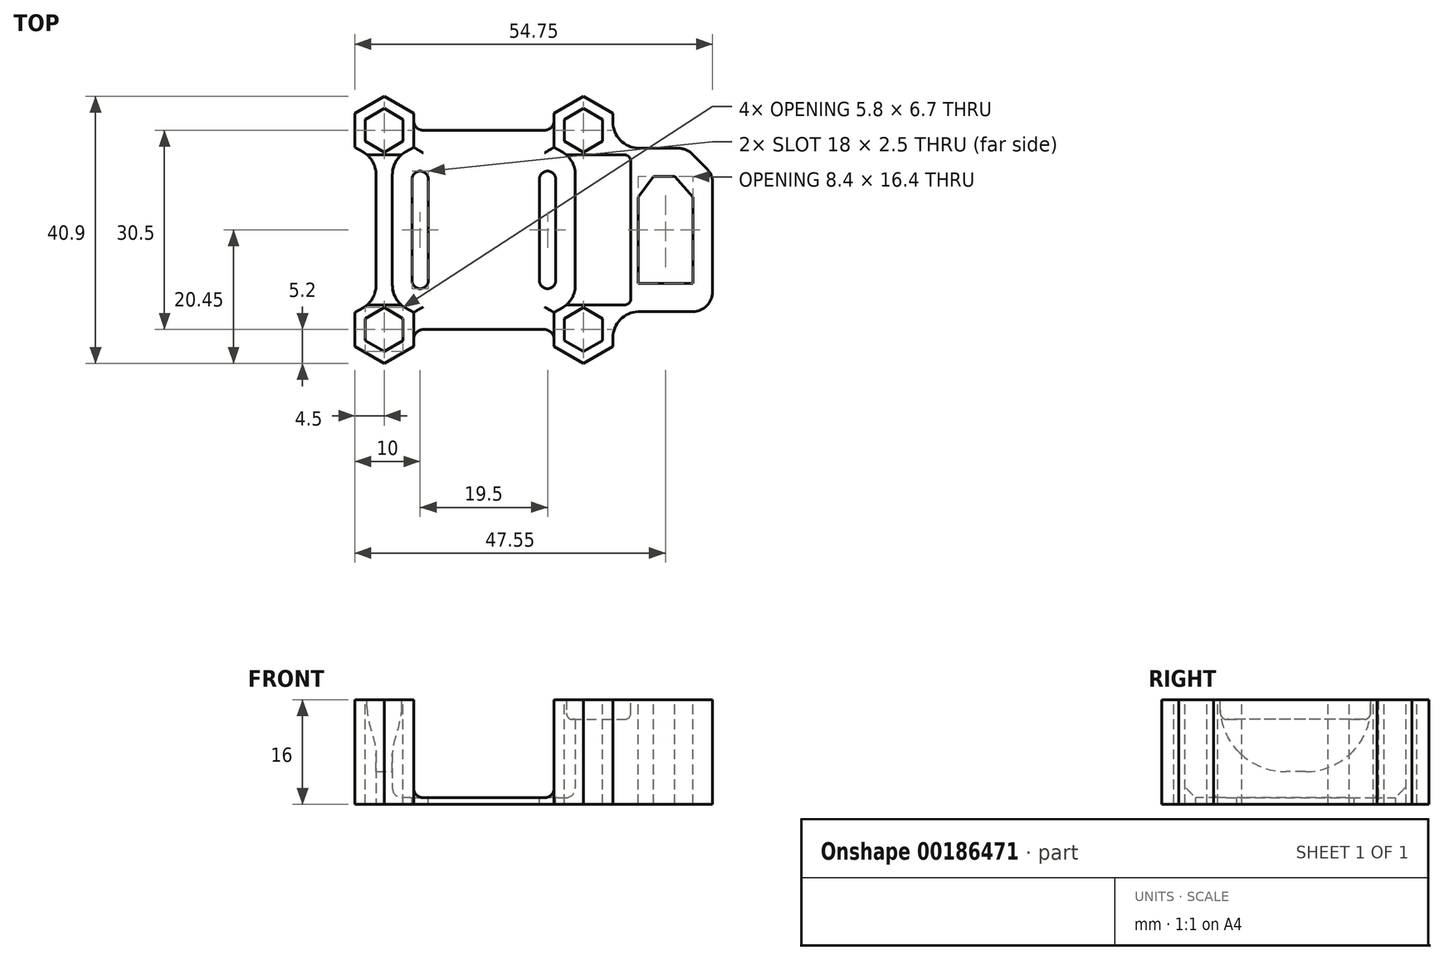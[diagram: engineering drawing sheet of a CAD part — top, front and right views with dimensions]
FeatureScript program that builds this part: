
annotation { "Feature Type Name" : "Feature", "Feature Type Description" : "" }
export const myFeature = defineFeature(function(context is Context, id is Id, definition is map)
    precondition{}
    {
        {
            var Q0;
            Q0=qCreatedBy(makeId("Top.planeOp"),FACE);
            var sketch = newSketch(context, id + "F0", { "sketchPlane" : qUnion([Q0])});
            skLineSegment(sketch, "E0.bottom", {"start": v(-15.25, 15.25) * mm, "end": v(15.25, 15.25) * mm});
            skLineSegment(sketch, "E0.top", {"start": v(-15.25, -15.25) * mm, "end": v(15.25, -15.25) * mm});
            skLineSegment(sketch, "E0.left", {"start": v(-15.25, 15.25) * mm, "end": v(-15.25, -15.25) * mm});
            skLineSegment(sketch, "E0.right", {"start": v(15.25, 15.25) * mm, "end": v(15.25, -15.25) * mm});
            skSolve(sketch);
        }
        {
            var Q0;
            Q0 = qSketchRegion(id + "F0", true);
            extrude(context, id + "F1", {"entities" : qUnion([Q0]), "depth" : 1 * mm});
        }
        {
            var Q0;
            Q0=qCreatedBy(makeId("Top.planeOp"),FACE);
            var sketch = newSketch(context, id + "F2", { "sketchPlane" : qUnion([Q0])});
            skCircle(sketch, "E1.cCircle", {"center": v(-15.25, 15.25) * mm, "radius": 4.5 * mm, "construction": true});
            skLineSegment(sketch, "E1.0", {"start": v(-16.5, 10.78) * mm, "end": v(-19.75, 12.65) * mm});
            skLineSegment(sketch, "E1.1", {"start": v(-19.75, 12.65) * mm, "end": v(-19.75, 17.85) * mm});
            skLineSegment(sketch, "E1.2", {"start": v(-19.75, 17.85) * mm, "end": v(-15.25, 20.45) * mm});
            skLineSegment(sketch, "E1.3", {"start": v(-15.25, 20.45) * mm, "end": v(-10.75, 17.85) * mm});
            skLineSegment(sketch, "E1.4", {"start": v(-10.75, 17.85) * mm, "end": v(-10.75, 12.65) * mm});
            skLineSegment(sketch, "E1.5", {"start": v(-10.75, 12.65) * mm, "end": v(-14, 10.78) * mm});
            skPoint(sketch, "E1.0.midPoint", {"position": v(-17.5, 11.35) * mm});
            skCircle(sketch, "E2.MirrorC", {"center": v(15.25, 15.25) * mm, "radius": 4.5 * mm, "construction": true});
            skLineSegment(sketch, "E3.MirrorCS", {"start": v(19.75, 12.65) * mm, "end": v(19.75, 17.85) * mm});
            skLineSegment(sketch, "E4.MirrorCS", {"start": v(19.75, 17.85) * mm, "end": v(15.25, 20.45) * mm});
            skLineSegment(sketch, "E5.MirrorCS", {"start": v(15.25, 20.45) * mm, "end": v(10.75, 17.85) * mm});
            skLineSegment(sketch, "E6.MirrorCS", {"start": v(10.75, 17.85) * mm, "end": v(10.75, 12.65) * mm});
            skLineSegment(sketch, "E7.MirrorCS", {"start": v(10.75, 12.65) * mm, "end": v(14, 10.78) * mm});
            skPoint(sketch, "E8.MirrorP", {"position": v(17.5, 11.35) * mm});
            skLineSegment(sketch, "E9.MirrorCS", {"start": v(-16.5, -10.78) * mm, "end": v(-19.75, -12.65) * mm});
            skLineSegment(sketch, "E10.MirrorCS", {"start": v(-19.75, -12.65) * mm, "end": v(-19.75, -17.85) * mm});
            skLineSegment(sketch, "E11.MirrorCS", {"start": v(10.75, -17.85) * mm, "end": v(10.75, -12.65) * mm});
            skLineSegment(sketch, "E12.MirrorCS", {"start": v(10.75, -12.65) * mm, "end": v(14, -10.78) * mm});
            skLineSegment(sketch, "E13.MirrorCS", {"start": v(-19.75, -17.85) * mm, "end": v(-15.25, -20.45) * mm});
            skLineSegment(sketch, "E14.MirrorCS", {"start": v(15.25, -20.45) * mm, "end": v(10.75, -17.85) * mm});
            skLineSegment(sketch, "E15.MirrorCS", {"start": v(-15.25, -20.45) * mm, "end": v(-10.75, -17.85) * mm});
            skLineSegment(sketch, "E16.MirrorCS", {"start": v(19.75, -17.85) * mm, "end": v(15.25, -20.45) * mm});
            skLineSegment(sketch, "E17.MirrorCS", {"start": v(-10.75, -17.85) * mm, "end": v(-10.75, -12.65) * mm});
            skLineSegment(sketch, "E18.MirrorCS", {"start": v(19.75, -12.65) * mm, "end": v(19.75, -17.85) * mm});
            skCircle(sketch, "E19.MirrorC", {"center": v(-15.25, -15.25) * mm, "radius": 4.5 * mm, "construction": true});
            skCircle(sketch, "E20.MirrorC", {"center": v(15.25, -15.25) * mm, "radius": 4.5 * mm, "construction": true});
            skPoint(sketch, "E21.MirrorP", {"position": v(17.5, -11.35) * mm});
            skLineSegment(sketch, "E22.MirrorCS", {"start": v(-10.75, -12.65) * mm, "end": v(-14, -10.78) * mm});
            skPoint(sketch, "E23.MirrorP", {"position": v(-17.5, -11.35) * mm});
            skLineSegment(sketch, "E24", {"start": v(-16.5, 10.78) * mm, "end": v(-16.5, -10.78) * mm});
            skLineSegment(sketch, "E25", {"start": v(-14, -10.78) * mm, "end": v(-14, 10.78) * mm});
            skLineSegment(sketch, "E26", {"start": v(14, 10.78) * mm, "end": v(14, -10.78) * mm});
            skPoint(sketch, "E27.orphan", {"position": v(-15.25, 10.05) * mm});
            skPoint(sketch, "E28.orphan", {"position": v(-15.25, -10.05) * mm});
            skPoint(sketch, "E29.orphan", {"position": v(15.25, -10.05) * mm});
            skPoint(sketch, "E30.orphan", {"position": v(15.25, 10.05) * mm});
            skLineSegment(sketch, "E31", {"start": v(24, 12.5) * mm, "end": v(24, -12.5) * mm, "construction": true});
            skLineSegment(sketch, "E32", {"start": v(24, -12.5) * mm, "end": v(19.75, -12.65) * mm});
            skLineSegment(sketch, "E33", {"start": v(24, 12.5) * mm, "end": v(19.75, 12.65) * mm});
            skLineSegment(sketch, "E34.bottom", {"start": v(24, 12.5) * mm, "end": v(35, 12.5) * mm});
            skLineSegment(sketch, "E34.top", {"start": v(24, -12.5) * mm, "end": v(35, -12.5) * mm});
            skLineSegment(sketch, "E34.right", {"start": v(35, 12.5) * mm, "end": v(35, -12.5) * mm});
            skSolve(sketch);
        }
        {
            var Q0;
            Q0 = qSketchRegion(id + "F2", true);
            extrude(context, id + "F3", {"entities" : qUnion([Q0]), "operationType" : NewBodyOperationType.ADD, "depth" : 16 * mm});
        }
        {
            var Q0;
            Q0=makeQuery(id+"F3.opExtrude","CAP_FACE",FACE,{"disambiguationData":[OSD([sQuery(id+"F2.wireOp",EDGE,"E3.MirrorCS"),sQuery(id+"F2.wireOp",EDGE,"E4.MirrorCS"),sQuery(id+"F2.wireOp",EDGE,"E5.MirrorCS"),sQuery(id+"F2.wireOp",EDGE,"E6.MirrorCS"),sQuery(id+"F2.wireOp",EDGE,"E7.MirrorCS"),sQuery(id+"F2.wireOp",EDGE,"E11.MirrorCS"),sQuery(id+"F2.wireOp",EDGE,"E12.MirrorCS"),sQuery(id+"F2.wireOp",EDGE,"E14.MirrorCS"),sQuery(id+"F2.wireOp",EDGE,"E16.MirrorCS"),sQuery(id+"F2.wireOp",EDGE,"E18.MirrorCS"),sQuery(id+"F2.wireOp",EDGE,"E26"),sQuery(id+"F2.wireOp",EDGE,"E31"),sQuery(id+"F2.wireOp",EDGE,"E32"),sQuery(id+"F2.wireOp",EDGE,"E33")])],"isStart":false});
            var sketch = newSketch(context, id + "F4", { "sketchPlane" : qUnion([Q0])});
            skLineSegment(sketch, "E35.bottom", {"start": v(-22.5, 11.5) * mm, "end": v(22.5, 11.5) * mm});
            skLineSegment(sketch, "E35.top", {"start": v(-22.5, -11.5) * mm, "end": v(22.5, -11.5) * mm});
            skLineSegment(sketch, "E35.left", {"start": v(-22.5, 11.5) * mm, "end": v(-22.5, -11.5) * mm});
            skLineSegment(sketch, "E35.right", {"start": v(22.5, 11.5) * mm, "end": v(22.5, -11.5) * mm});
            skPoint(sketch, "E36.visualSharp", {"position": v(22.5, 11.5) * mm});
            skPoint(sketch, "E37.visualSharp", {"position": v(22.5, -11.5) * mm});
            skSolve(sketch);
        }
        {
            var Q0;
            Q0 = qSketchRegion(id + "F4", true);
            extrude(context, id + "F5", {"entities" : qUnion([Q0]), "operationType" : NewBodyOperationType.REMOVE, "oppositeDirection" : true, "depth" : 3 * mm});
        }
        {
            var Q0;
            {var subQ0=sQuery(id+"F2.wireOp",EDGE,"E34.top");var subQ1=sQuery(id+"F2.wireOp",EDGE,"E34.bottom");var subQ2=sQuery(id+"F2.wireOp",EDGE,"E33");var subQ3=sQuery(id+"F2.wireOp",EDGE,"E32");var subQ4=sQuery(id+"F2.wireOp",EDGE,"E34.right");Q0=makeQuery(id+"F5.boolean.opBoolean","SPLIT",FACE,{"disambiguationData":[TD([makeQuery(id+"F3.opExtrude","SWEPT_FACE",FACE,{"disambiguationData":[OSD([subQ3])]})])],"derivedFrom":makeQuery(id+"F3.opExtrude","CAP_FACE",FACE,{"disambiguationData":[OSD([sQuery(id+"F2.wireOp",EDGE,"E3.MirrorCS"),sQuery(id+"F2.wireOp",EDGE,"E4.MirrorCS"),sQuery(id+"F2.wireOp",EDGE,"E5.MirrorCS"),sQuery(id+"F2.wireOp",EDGE,"E6.MirrorCS"),sQuery(id+"F2.wireOp",EDGE,"E7.MirrorCS"),sQuery(id+"F2.wireOp",EDGE,"E11.MirrorCS"),sQuery(id+"F2.wireOp",EDGE,"E12.MirrorCS"),sQuery(id+"F2.wireOp",EDGE,"E14.MirrorCS"),sQuery(id+"F2.wireOp",EDGE,"E16.MirrorCS"),sQuery(id+"F2.wireOp",EDGE,"E18.MirrorCS"),sQuery(id+"F2.wireOp",EDGE,"E26"),subQ3,subQ2,subQ1,subQ0,subQ4])],"isStart":false})});}
            var sketch = newSketch(context, id + "F6", { "sketchPlane" : qUnion([Q0])});
            skLineSegment(sketch, "E38.bottom", {"start": v(26, 8.2) * mm, "end": v(29.2, 8.2) * mm});
            skLineSegment(sketch, "E38.top", {"start": v(23.6, -8.2) * mm, "end": v(32, -8.2) * mm});
            skLineSegment(sketch, "E38.left", {"start": v(23.6, 5) * mm, "end": v(23.6, -8.2) * mm});
            skLineSegment(sketch, "E38.right", {"start": v(32, 5) * mm, "end": v(32, -8.2) * mm});
            skLineSegment(sketch, "E39", {"start": v(26, 8.2) * mm, "end": v(23.6, 5) * mm});
            skLineSegment(sketch, "E40", {"start": v(29.2, 8.2) * mm, "end": v(32, 5) * mm});
            skCircle(sketch, "E41.cCircle", {"center": v(-15.25, 15.25) * mm, "radius": 2.9 * mm, "construction": true});
            skLineSegment(sketch, "E41.0", {"start": v(-12.35, 13.58) * mm, "end": v(-15.25, 11.9) * mm});
            skLineSegment(sketch, "E41.1", {"start": v(-15.25, 11.9) * mm, "end": v(-18.15, 13.58) * mm});
            skLineSegment(sketch, "E41.2", {"start": v(-18.15, 13.58) * mm, "end": v(-18.15, 16.92) * mm});
            skLineSegment(sketch, "E41.3", {"start": v(-18.15, 16.92) * mm, "end": v(-15.25, 18.6) * mm});
            skLineSegment(sketch, "E41.4", {"start": v(-15.25, 18.6) * mm, "end": v(-12.35, 16.92) * mm});
            skLineSegment(sketch, "E41.5", {"start": v(-12.35, 16.92) * mm, "end": v(-12.35, 13.58) * mm});
            skPoint(sketch, "E41.0.midPoint", {"position": v(-13.8, 12.74) * mm});
            skLineSegment(sketch, "E42.0.1.0", {"start": v(-15.25, -11.9) * mm, "end": v(-12.35, -13.58) * mm});
            skLineSegment(sketch, "E42.0.1.1", {"start": v(-15.25, -18.6) * mm, "end": v(-18.15, -16.92) * mm});
            skLineSegment(sketch, "E42.0.1.2", {"start": v(-18.15, -13.58) * mm, "end": v(-15.25, -11.9) * mm});
            skPoint(sketch, "E42.0.1.3", {"position": v(-13.8, -17.76) * mm});
            skCircle(sketch, "E42.0.1.4", {"center": v(-15.25, -15.25) * mm, "radius": 2.9 * mm, "construction": true});
            skLineSegment(sketch, "E42.0.1.5", {"start": v(-12.35, -13.58) * mm, "end": v(-12.35, -16.92) * mm});
            skLineSegment(sketch, "E42.0.1.6", {"start": v(-18.15, -16.92) * mm, "end": v(-18.15, -13.58) * mm});
            skLineSegment(sketch, "E42.0.1.7", {"start": v(-12.35, -16.92) * mm, "end": v(-15.25, -18.6) * mm});
            skLineSegment(sketch, "E42.direction1", {"start": v(-18.15, 13.58) * mm, "end": v(12.35, 13.58) * mm, "construction": true});
            skLineSegment(sketch, "E42.direction2", {"start": v(-18.15, 13.58) * mm, "end": v(-18.15, -16.92) * mm, "construction": true});
            skLineSegment(sketch, "E43.MirrorCS", {"start": v(12.35, 16.92) * mm, "end": v(12.35, 13.58) * mm});
            skLineSegment(sketch, "E44.MirrorCS", {"start": v(18.15, 16.92) * mm, "end": v(15.25, 18.6) * mm});
            skLineSegment(sketch, "E45.MirrorCS", {"start": v(12.35, -16.92) * mm, "end": v(15.25, -18.6) * mm});
            skLineSegment(sketch, "E46.MirrorCS", {"start": v(18.15, 13.58) * mm, "end": v(18.15, 16.92) * mm});
            skLineSegment(sketch, "E47.MirrorCS", {"start": v(15.25, 11.9) * mm, "end": v(18.15, 13.58) * mm});
            skLineSegment(sketch, "E48.MirrorCS", {"start": v(12.35, 13.58) * mm, "end": v(15.25, 11.9) * mm});
            skLineSegment(sketch, "E49.MirrorCS", {"start": v(18.15, -13.58) * mm, "end": v(15.25, -11.9) * mm});
            skLineSegment(sketch, "E50.MirrorCS", {"start": v(15.25, -11.9) * mm, "end": v(12.35, -13.58) * mm});
            skLineSegment(sketch, "E51.MirrorCS", {"start": v(12.35, -13.58) * mm, "end": v(12.35, -16.92) * mm});
            skLineSegment(sketch, "E52.MirrorCS", {"start": v(18.15, -16.92) * mm, "end": v(18.15, -13.58) * mm});
            skLineSegment(sketch, "E53.MirrorCS", {"start": v(15.25, 18.6) * mm, "end": v(12.35, 16.92) * mm});
            skCircle(sketch, "E54.MirrorC", {"center": v(15.25, -15.25) * mm, "radius": 2.9 * mm, "construction": true});
            skLineSegment(sketch, "E55.MirrorCS", {"start": v(15.25, -18.6) * mm, "end": v(18.15, -16.92) * mm});
            skPoint(sketch, "E56.MirrorP", {"position": v(13.8, -17.76) * mm});
            skLineSegment(sketch, "E57.MirrorCS", {"start": v(18.15, 13.58) * mm, "end": v(18.15, -16.92) * mm, "construction": true});
            skPoint(sketch, "E58.MirrorP", {"position": v(13.8, 12.74) * mm});
            skCircle(sketch, "E59.MirrorC", {"center": v(15.25, 15.25) * mm, "radius": 2.9 * mm, "construction": true});
            skSolve(sketch);
        }
        {
            var Q0;
            Q0 = qSketchRegion(id + "F6", true);
            extrude(context, id + "F7", {"entities" : qUnion([Q0]), "operationType" : NewBodyOperationType.REMOVE, "endBound" : BoundingType.THROUGH_ALL, "oppositeDirection" : true, "depth" : 25 * mm});
        }
        {
            var Q0;
            Q0=makeQuery(id+"F3.opExtrude","SWEPT_EDGE",EDGE,{"disambiguationData":[OSD([sQuery(id+"F2.wireOp",EDGE,"E34.bottom"),sQuery(id+"F2.wireOp",EDGE,"E34.right")])]});
            chamfer(context, id + "F8", {"entities" : qUnion([Q0]), "width" : 4 * mm, "tangentPropagation" : true});
        }
        {
            var Q0;
            Q0=makeQuery(id+"F3.opExtrude","SWEPT_EDGE",EDGE,{"disambiguationData":[OSD([sQuery(id+"F2.wireOp",EDGE,"E1.0"),sQuery(id+"F2.wireOp",EDGE,"E24")])]});
            var Q1;
            Q1=makeQuery(id+"F3.opExtrude","SWEPT_EDGE",EDGE,{"disambiguationData":[OSD([sQuery(id+"F2.wireOp",EDGE,"E9.MirrorCS"),sQuery(id+"F2.wireOp",EDGE,"E24")])]});
            var Q2;
            Q2=makeQuery(id+"F3.opExtrude","SWEPT_EDGE",EDGE,{"disambiguationData":[OSD([sQuery(id+"F2.wireOp",EDGE,"E1.5"),sQuery(id+"F2.wireOp",EDGE,"E25")])]});
            var Q3;
            Q3=makeQuery(id+"F3.opExtrude","SWEPT_EDGE",EDGE,{"disambiguationData":[OSD([sQuery(id+"F2.wireOp",EDGE,"E22.MirrorCS"),sQuery(id+"F2.wireOp",EDGE,"E25")])]});
            var Q4;
            Q4=makeQuery(id+"F3.opExtrude","SWEPT_EDGE",EDGE,{"disambiguationData":[OSD([sQuery(id+"F2.wireOp",EDGE,"E7.MirrorCS"),sQuery(id+"F2.wireOp",EDGE,"E26")])]});
            var Q5;
            Q5=makeQuery(id+"F3.opExtrude","SWEPT_EDGE",EDGE,{"disambiguationData":[OSD([sQuery(id+"F2.wireOp",EDGE,"E12.MirrorCS"),sQuery(id+"F2.wireOp",EDGE,"E26")])]});
            var Q6;
            Q6=makeQuery(id+"F3.opExtrude","SWEPT_EDGE",EDGE,{"disambiguationData":[OSD([sQuery(id+"F2.wireOp",EDGE,"E33"),sQuery(id+"F2.wireOp",EDGE,"E34.bottom")])]});
            var Q7;
            Q7=makeQuery(id+"F3.opExtrude","SWEPT_EDGE",EDGE,{"disambiguationData":[OSD([sQuery(id+"F2.wireOp",EDGE,"E3.MirrorCS"),sQuery(id+"F2.wireOp",EDGE,"E33")])]});
            var Q8;
            Q8=makeQuery(id+"F3.opExtrude","SWEPT_EDGE",EDGE,{"disambiguationData":[OSD([sQuery(id+"F2.wireOp",EDGE,"E18.MirrorCS"),sQuery(id+"F2.wireOp",EDGE,"E32")])]});
            var Q9;
            Q9=makeQuery(id+"F3.opExtrude","SWEPT_EDGE",EDGE,{"disambiguationData":[OSD([sQuery(id+"F2.wireOp",EDGE,"E32"),sQuery(id+"F2.wireOp",EDGE,"E34.top")])]});
            fillet(context, id + "F9", {"entities" : qUnion([Q0, Q1, Q2, Q3, Q4, Q5, Q6, Q7, Q8, Q9]), "radius" : 4 * mm, "tangentPropagation" : true, "allowEdgeOverflow" : false});
        }
        {
            var Q0;
            {var subQ1=sQuery(id+"F4.wireOp",EDGE,"E35.bottom");Q0=makeQuery(id+"F5.boolean.opBoolean","COPY",EDGE,{"disambiguationData":[TD([makeQuery(id+"F3.opExtrude","SWEPT_FACE",FACE,{"disambiguationData":[OSD([sQuery(id+"F2.wireOp",EDGE,"E3.MirrorCS")])]})])],"derivedFrom":makeQuery(id+"F5.opExtrude","CAP_EDGE",EDGE,{"disambiguationData":[OSD([subQ1])],"isStart":false})});}
            var Q1;
            {var subQ0=sQuery(id+"F4.wireOp",EDGE,"E35.top");Q1=makeQuery(id+"F5.boolean.opBoolean","COPY",EDGE,{"disambiguationData":[TD([makeQuery(id+"F3.opExtrude","SWEPT_FACE",FACE,{"disambiguationData":[OSD([sQuery(id+"F2.wireOp",EDGE,"E12.MirrorCS")])]})])],"derivedFrom":makeQuery(id+"F5.opExtrude","CAP_EDGE",EDGE,{"disambiguationData":[OSD([subQ0])],"isStart":false})});}
            var Q2;
            Q2=makeQuery(id+"F5.boolean.opBoolean","COPY",EDGE,{"derivedFrom":makeQuery(id+"F5.opExtrude","CAP_EDGE",EDGE,{"disambiguationData":[OSD([sQuery(id+"F4.wireOp",EDGE,"E35.right")])],"isStart":false})});
            var Q3;
            {var subQ0=sQuery(id+"F4.wireOp",EDGE,"E35.bottom");Q3=makeQuery(id+"F5.boolean.opBoolean","COPY",EDGE,{"disambiguationData":[TD([makeQuery(id+"F3.opExtrude","SWEPT_FACE",FACE,{"disambiguationData":[OSD([sQuery(id+"F2.wireOp",EDGE,"E7.MirrorCS")])]})])],"derivedFrom":makeQuery(id+"F5.opExtrude","CAP_EDGE",EDGE,{"disambiguationData":[OSD([subQ0])],"isStart":false})});}
            fillet(context, id + "F10", {"entities" : qUnion([Q0, Q1, Q2, Q3]), "radius" : 1 * mm, "tangentPropagation" : true, "allowEdgeOverflow" : false});
        }
        {
            var Q0;
            Q0=makeQuery(id+"F9.opFillet","BLEND_EDGE",EDGE,{"blendedFrom":[makeQuery(id+"F3.opExtrude","SWEPT_EDGE",EDGE,{"disambiguationData":[OSD([sQuery(id+"F2.wireOp",EDGE,"E22.MirrorCS"),sQuery(id+"F2.wireOp",EDGE,"E25")])]}),makeQuery(id+"F1.opExtrude","CAP_FACE",FACE,{"disambiguationData":[OSD([sQuery(id+"F0.wireOp",EDGE,"E0.bottom"),sQuery(id+"F0.wireOp",EDGE,"E0.top"),sQuery(id+"F0.wireOp",EDGE,"E0.left"),sQuery(id+"F0.wireOp",EDGE,"E0.right")])],"isStart":false})],"blendedInto":[makeQuery(id+"F1.opExtrude","CAP_FACE",FACE,{"disambiguationData":[OSD([sQuery(id+"F0.wireOp",EDGE,"E0.bottom"),sQuery(id+"F0.wireOp",EDGE,"E0.top"),sQuery(id+"F0.wireOp",EDGE,"E0.left"),sQuery(id+"F0.wireOp",EDGE,"E0.right")])],"isStart":false})]});
            var Q1;
            Q1=makeQuery(id+"F3.boolean.opBoolean","INTERSECT",EDGE,{"derivedFrom":[makeQuery(id+"F1.opExtrude","CAP_FACE",FACE,{"disambiguationData":[OSD([sQuery(id+"F0.wireOp",EDGE,"E0.bottom"),sQuery(id+"F0.wireOp",EDGE,"E0.top"),sQuery(id+"F0.wireOp",EDGE,"E0.left"),sQuery(id+"F0.wireOp",EDGE,"E0.right")])],"isStart":false}),makeQuery(id+"F3.opExtrude","SWEPT_FACE",FACE,{"disambiguationData":[OSD([sQuery(id+"F2.wireOp",EDGE,"E17.MirrorCS")])]})]});
            var Q2;
            Q2=makeQuery(id+"F3.boolean.opBoolean","INTERSECT",EDGE,{"derivedFrom":[makeQuery(id+"F1.opExtrude","CAP_FACE",FACE,{"disambiguationData":[OSD([sQuery(id+"F0.wireOp",EDGE,"E0.bottom"),sQuery(id+"F0.wireOp",EDGE,"E0.top"),sQuery(id+"F0.wireOp",EDGE,"E0.left"),sQuery(id+"F0.wireOp",EDGE,"E0.right")])],"isStart":false}),makeQuery(id+"F3.opExtrude","SWEPT_FACE",FACE,{"disambiguationData":[OSD([sQuery(id+"F2.wireOp",EDGE,"E1.4")])]})]});
            var Q3;
            Q3=makeQuery(id+"F3.boolean.opBoolean","INTERSECT",EDGE,{"derivedFrom":[makeQuery(id+"F1.opExtrude","CAP_FACE",FACE,{"disambiguationData":[OSD([sQuery(id+"F0.wireOp",EDGE,"E0.bottom"),sQuery(id+"F0.wireOp",EDGE,"E0.top"),sQuery(id+"F0.wireOp",EDGE,"E0.left"),sQuery(id+"F0.wireOp",EDGE,"E0.right")])],"isStart":false}),makeQuery(id+"F3.opExtrude","SWEPT_FACE",FACE,{"disambiguationData":[OSD([sQuery(id+"F2.wireOp",EDGE,"E26")])]})]});
            var Q4;
            Q4=makeQuery(id+"F3.boolean.opBoolean","INTERSECT",EDGE,{"derivedFrom":[makeQuery(id+"F1.opExtrude","CAP_FACE",FACE,{"disambiguationData":[OSD([sQuery(id+"F0.wireOp",EDGE,"E0.bottom"),sQuery(id+"F0.wireOp",EDGE,"E0.top"),sQuery(id+"F0.wireOp",EDGE,"E0.left"),sQuery(id+"F0.wireOp",EDGE,"E0.right")])],"isStart":false}),makeQuery(id+"F3.opExtrude","SWEPT_FACE",FACE,{"disambiguationData":[OSD([sQuery(id+"F2.wireOp",EDGE,"E6.MirrorCS")])]})]});
            var Q5;
            Q5=makeQuery(id+"F3.boolean.opBoolean","INTERSECT",EDGE,{"derivedFrom":[makeQuery(id+"F1.opExtrude","CAP_FACE",FACE,{"disambiguationData":[OSD([sQuery(id+"F0.wireOp",EDGE,"E0.bottom"),sQuery(id+"F0.wireOp",EDGE,"E0.top"),sQuery(id+"F0.wireOp",EDGE,"E0.left"),sQuery(id+"F0.wireOp",EDGE,"E0.right")])],"isStart":false}),makeQuery(id+"F3.opExtrude","SWEPT_FACE",FACE,{"disambiguationData":[OSD([sQuery(id+"F2.wireOp",EDGE,"E11.MirrorCS")])]})]});
            fillet(context, id + "F11", {"entities" : qUnion([Q0, Q1, Q2, Q3, Q4, Q5]), "radius" : 1.5 * mm, "tangentPropagation" : true, "allowEdgeOverflow" : false});
        }
        {
            var Q0;
            Q0=makeQuery(id+"F5.boolean.opBoolean","COPY",EDGE,{"derivedFrom":makeQuery(id+"F5.opExtrude","SWEPT_EDGE",EDGE,{"disambiguationData":[OSD([sQuery(id+"F4.wireOp",EDGE,"E35.bottom"),sQuery(id+"F4.wireOp",EDGE,"E35.right")])]})});
            var Q1;
            Q1=makeQuery(id+"F5.boolean.opBoolean","COPY",EDGE,{"derivedFrom":makeQuery(id+"F5.opExtrude","SWEPT_EDGE",EDGE,{"disambiguationData":[OSD([sQuery(id+"F4.wireOp",EDGE,"E35.top"),sQuery(id+"F4.wireOp",EDGE,"E35.right")])]})});
            fillet(context, id + "F12", {"entities" : qUnion([Q0, Q1]), "radius" : 1 * mm, "tangentPropagation" : true, "allowEdgeOverflow" : false});
        }
        {
            var Q0;
            Q0=makeQuery(id+"F3.opExtrude","SWEPT_EDGE",EDGE,{"disambiguationData":[OSD([sQuery(id+"F2.wireOp",EDGE,"E34.top"),sQuery(id+"F2.wireOp",EDGE,"E34.right")])]});
            var Q1;
            {var subQ0=sQuery(id+"F2.wireOp",EDGE,"E34.right");Q1=makeQuery(id+"F8.opChamfer","BLEND_EDGE",EDGE,{"blendedFrom":[makeQuery(id+"F3.opExtrude","SWEPT_EDGE",EDGE,{"disambiguationData":[OSD([sQuery(id+"F2.wireOp",EDGE,"E34.bottom"),subQ0])]}),makeQuery(id+"F3.opExtrude","SWEPT_FACE",FACE,{"disambiguationData":[OSD([subQ0])]})],"blendedInto":[makeQuery(id+"F3.opExtrude","SWEPT_FACE",FACE,{"disambiguationData":[OSD([subQ0])]})]});}
            var Q2;
            {var subQ0=sQuery(id+"F2.wireOp",EDGE,"E34.bottom");Q2=makeQuery(id+"F8.opChamfer","BLEND_EDGE",EDGE,{"blendedFrom":[makeQuery(id+"F3.opExtrude","SWEPT_EDGE",EDGE,{"disambiguationData":[OSD([subQ0,sQuery(id+"F2.wireOp",EDGE,"E34.right")])]}),makeQuery(id+"F3.opExtrude","SWEPT_FACE",FACE,{"disambiguationData":[OSD([subQ0])]})],"blendedInto":[makeQuery(id+"F3.opExtrude","SWEPT_FACE",FACE,{"disambiguationData":[OSD([subQ0])]})]});}
            fillet(context, id + "F13", {"entities" : qUnion([Q0, Q1, Q2]), "radius" : 3 * mm, "tangentPropagation" : true, "allowEdgeOverflow" : false});
        }
        {
            var Q0;
            Q0=makeQuery(id+"F3.boolean.opBoolean","INTERSECT",EDGE,{"derivedFrom":[makeQuery(id+"F1.opExtrude","SWEPT_FACE",FACE,{"disambiguationData":[OSD([sQuery(id+"F0.wireOp",EDGE,"E0.bottom")])]}),makeQuery(id+"F3.opExtrude","SWEPT_FACE",FACE,{"disambiguationData":[OSD([sQuery(id+"F2.wireOp",EDGE,"E6.MirrorCS")])]})]});
            var Q1;
            Q1=makeQuery(id+"F3.boolean.opBoolean","INTERSECT",EDGE,{"derivedFrom":[makeQuery(id+"F1.opExtrude","SWEPT_FACE",FACE,{"disambiguationData":[OSD([sQuery(id+"F0.wireOp",EDGE,"E0.bottom")])]}),makeQuery(id+"F3.opExtrude","SWEPT_FACE",FACE,{"disambiguationData":[OSD([sQuery(id+"F2.wireOp",EDGE,"E1.4")])]})]});
            var Q2;
            Q2=makeQuery(id+"F3.boolean.opBoolean","INTERSECT",EDGE,{"derivedFrom":[makeQuery(id+"F1.opExtrude","SWEPT_FACE",FACE,{"disambiguationData":[OSD([sQuery(id+"F0.wireOp",EDGE,"E0.top")])]}),makeQuery(id+"F3.opExtrude","SWEPT_FACE",FACE,{"disambiguationData":[OSD([sQuery(id+"F2.wireOp",EDGE,"E17.MirrorCS")])]})]});
            var Q3;
            Q3=makeQuery(id+"F3.boolean.opBoolean","INTERSECT",EDGE,{"derivedFrom":[makeQuery(id+"F1.opExtrude","SWEPT_FACE",FACE,{"disambiguationData":[OSD([sQuery(id+"F0.wireOp",EDGE,"E0.top")])]}),makeQuery(id+"F3.opExtrude","SWEPT_FACE",FACE,{"disambiguationData":[OSD([sQuery(id+"F2.wireOp",EDGE,"E11.MirrorCS")])]})]});
            fillet(context, id + "F14", {"entities" : qUnion([Q0, Q1, Q2, Q3]), "radius" : 1.5 * mm, "tangentPropagation" : true, "allowEdgeOverflow" : false});
        }
        {
            var Q0;
            {var subQ0=sQuery(id+"F4.wireOp",EDGE,"E35.bottom");var subQ1=sQuery(id+"F4.wireOp",EDGE,"E35.left");var subQ2=sQuery(id+"F4.wireOp",EDGE,"E35.top");Q0=makeQuery(id+"F5.boolean.opBoolean","COPY",FACE,{"disambiguationData":[TD([makeQuery(id+"F3.opExtrude","SWEPT_FACE",FACE,{"disambiguationData":[OSD([sQuery(id+"F2.wireOp",EDGE,"E1.0")])]})])],"derivedFrom":makeQuery(id+"F5.opExtrude","CAP_FACE",FACE,{"disambiguationData":[OSD([subQ0,subQ2,subQ1,sQuery(id+"F4.wireOp",EDGE,"E35.right")])],"isStart":false})});}
            var sketch = newSketch(context, id + "F15", { "sketchPlane" : qUnion([Q0])});
            skLineSegment(sketch, "E60.bottom", {"start": v(-12.6, 11.5) * mm, "end": v(-17.9, 11.5) * mm});
            skLineSegment(sketch, "E60.top", {"start": v(-12.6, -11.5) * mm, "end": v(-17.9, -11.5) * mm});
            skLineSegment(sketch, "E60.left", {"start": v(-12.6, 11.5) * mm, "end": v(-12.6, -11.5) * mm});
            skLineSegment(sketch, "E60.right", {"start": v(-17.9, 11.5) * mm, "end": v(-17.9, -11.5) * mm});
            skSolve(sketch);
        }
        {
            var Q0;
            Q0 = qSketchRegion(id + "F15", true);
            extrude(context, id + "F16", {"entities" : qUnion([Q0]), "operationType" : NewBodyOperationType.REMOVE, "oppositeDirection" : true, "depth" : 8 * mm});
        }
        {
            var Q0;
            Q0=makeQuery(id+"F16.boolean.opBoolean","COPY",EDGE,{"derivedFrom":makeQuery(id+"F16.opExtrude","CAP_EDGE",EDGE,{"disambiguationData":[OSD([sQuery(id+"F15.wireOp",EDGE,"E60.bottom")])],"isStart":false})});
            var Q1;
            Q1=makeQuery(id+"F16.boolean.opBoolean","COPY",EDGE,{"derivedFrom":makeQuery(id+"F16.opExtrude","CAP_EDGE",EDGE,{"disambiguationData":[OSD([sQuery(id+"F15.wireOp",EDGE,"E60.top")])],"isStart":false})});
            fillet(context, id + "F17", {"entities" : qUnion([Q0, Q1]), "radius" : 10 * mm, "tangentPropagation" : true, "allowEdgeOverflow" : false});
        }
        {
            var Q0;
            Q0=makeQuery(id+"F1.opExtrude","CAP_FACE",FACE,{"disambiguationData":[OSD([sQuery(id+"F0.wireOp",EDGE,"E0.bottom"),sQuery(id+"F0.wireOp",EDGE,"E0.top"),sQuery(id+"F0.wireOp",EDGE,"E0.left"),sQuery(id+"F0.wireOp",EDGE,"E0.right")])],"isStart":false});
            var sketch = newSketch(context, id + "F18", { "sketchPlane" : qUnion([Q0])});
            skLineSegment(sketch, "E61.bottom", {"start": v(-9.75, 9) * mm, "end": v(-9.75, 9) * mm});
            skLineSegment(sketch, "E61.top", {"start": v(-9.75, -9) * mm, "end": v(-9.75, -9) * mm});
            skLineSegment(sketch, "E61.left", {"start": v(-11, 7.75) * mm, "end": v(-11, -7.75) * mm});
            skLineSegment(sketch, "E61.right", {"start": v(-8.5, 7.75) * mm, "end": v(-8.5, -7.75) * mm});
            skPoint(sketch, "E62.visualSharp", {"position": v(-11, 9) * mm});
            skArc(sketch, "E62.filletArc", {"start": v(-9.75, 9) * mm, "mid": v(-10.63, 8.63) * mm, "end": v(-11, 7.75) * mm});
            skPoint(sketch, "E63.visualSharp", {"position": v(-8.5, 9) * mm});
            skArc(sketch, "E63.filletArc", {"start": v(-8.5, 7.75) * mm, "mid": v(-8.87, 8.63) * mm, "end": v(-9.75, 9) * mm});
            skPoint(sketch, "E64.visualSharp", {"position": v(-11, -9) * mm});
            skArc(sketch, "E64.filletArc", {"start": v(-11, -7.75) * mm, "mid": v(-10.63, -8.63) * mm, "end": v(-9.75, -9) * mm});
            skPoint(sketch, "E65.visualSharp", {"position": v(-8.5, -9) * mm});
            skArc(sketch, "E65.filletArc", {"start": v(-9.75, -9) * mm, "mid": v(-8.87, -8.63) * mm, "end": v(-8.5, -7.75) * mm});
            skArc(sketch, "E66.MirrorCS", {"start": v(9.75, 9) * mm, "mid": v(10.63, 8.63) * mm, "end": v(11, 7.75) * mm});
            skArc(sketch, "E67.MirrorCS", {"start": v(8.5, 7.75) * mm, "mid": v(8.87, 8.63) * mm, "end": v(9.75, 9) * mm});
            skArc(sketch, "E68.MirrorCS", {"start": v(11, -7.75) * mm, "mid": v(10.63, -8.63) * mm, "end": v(9.75, -9) * mm});
            skArc(sketch, "E69.MirrorCS", {"start": v(9.75, -9) * mm, "mid": v(8.87, -8.63) * mm, "end": v(8.5, -7.75) * mm});
            skPoint(sketch, "E70.MirrorP", {"position": v(11, -9) * mm});
            skPoint(sketch, "E71.MirrorP", {"position": v(8.5, 9) * mm});
            skPoint(sketch, "E72.MirrorP", {"position": v(8.5, -9) * mm});
            skLineSegment(sketch, "E73.MirrorCS", {"start": v(8.5, 7.75) * mm, "end": v(8.5, -7.75) * mm});
            skLineSegment(sketch, "E74.MirrorCS", {"start": v(11, 7.75) * mm, "end": v(11, -7.75) * mm});
            skPoint(sketch, "E75.MirrorP", {"position": v(11, 9) * mm});
            skLineSegment(sketch, "E76.MirrorCS", {"start": v(9.75, 9) * mm, "end": v(9.75, 9) * mm});
            skLineSegment(sketch, "E77.MirrorCS", {"start": v(9.75, -9) * mm, "end": v(9.75, -9) * mm});
            skSolve(sketch);
        }
        {
            var Q0;
            Q0 = qSketchRegion(id + "F18", true);
            extrude(context, id + "F19", {"entities" : qUnion([Q0]), "operationType" : NewBodyOperationType.REMOVE, "endBound" : BoundingType.THROUGH_ALL, "oppositeDirection" : true, "depth" : 25 * mm});
        }
    });
